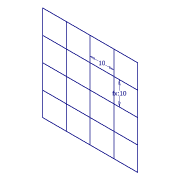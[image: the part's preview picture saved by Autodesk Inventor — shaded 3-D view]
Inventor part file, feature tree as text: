
AUTODESK INVENTOR PART (.ipt)
format: ipt  version: 2016 (Build 200138000, 138)  size: 124,416 bytes
history: native  units: in
note: dims shown in document units (in); Inventor stores cm internally (conversion verified against a paired STEP export)
features: plane x8, sketch x1
ambient origin geometry x8: Origin, YZ Plane, XZ Plane, XY Plane, X Axis, Y Axis, Z Axis, Center Point
feature tree (9):
  sketch  "Sketch1"  dims[d1=0.3937in d2=0.7874in d3=0.3937in d4=-0.7874in d5=-0.3937in]
  plane  "Work Plane1"
  plane  "Work Plane2"
  plane  "Work Plane3"
  plane  "Work Plane4"
  plane  "Work Plane5"
  plane  "Work Plane6"
  plane  "Work Plane7"
  plane  "Work Plane8"
